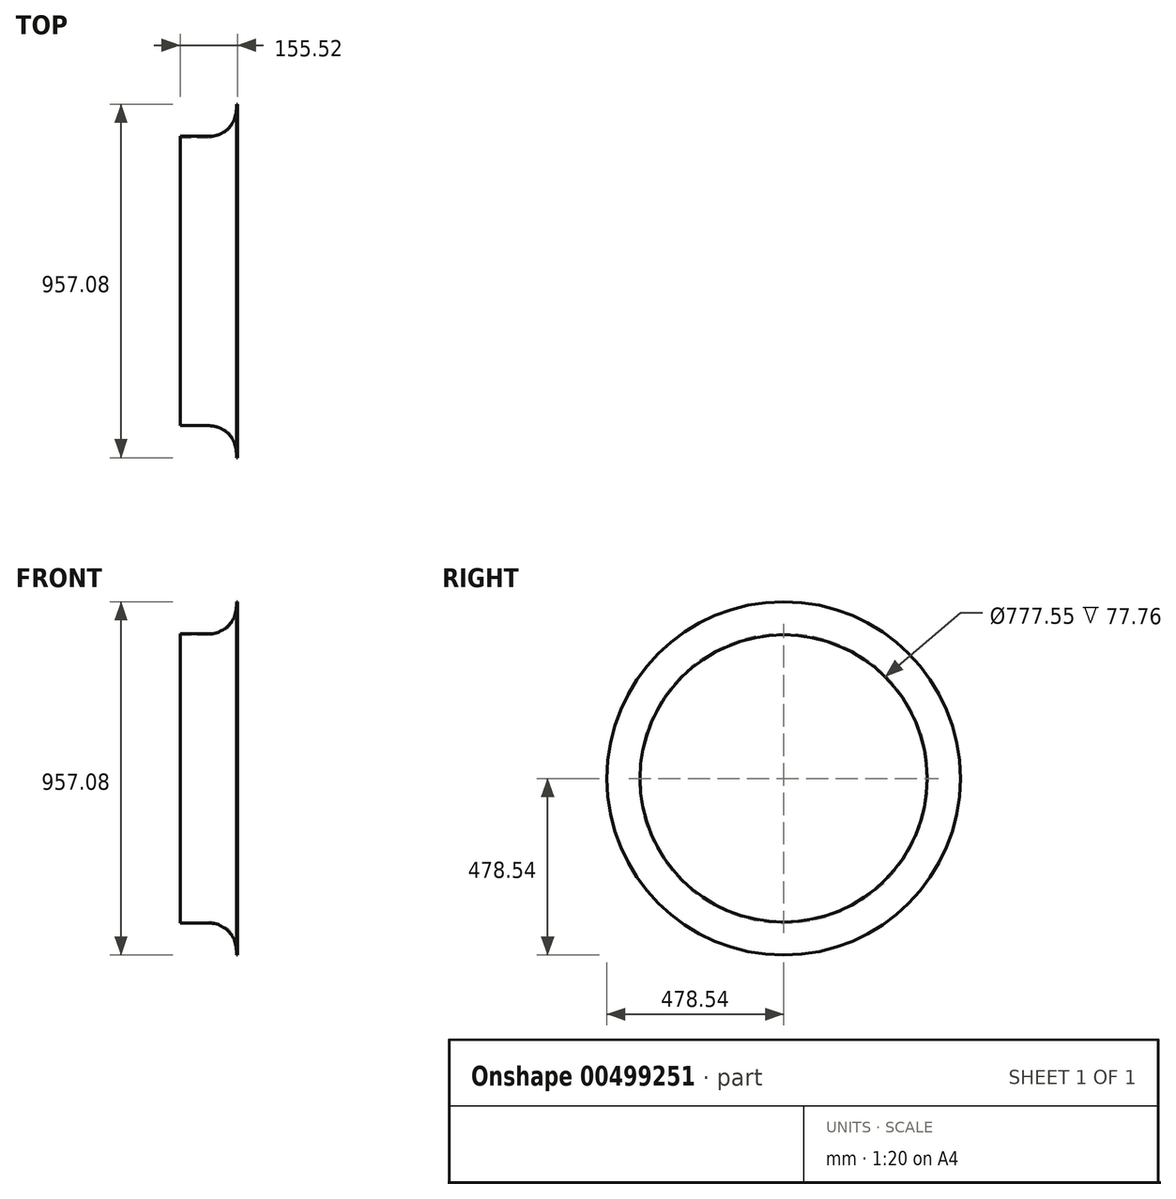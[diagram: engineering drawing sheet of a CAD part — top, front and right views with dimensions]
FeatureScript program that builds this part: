
annotation { "Feature Type Name" : "Feature", "Feature Type Description" : "" }
export const myFeature = defineFeature(function(context is Context, id is Id, definition is map)
    precondition{}
    {
        {
            var Q0;
            Q0=qCreatedBy(makeId("Front.planeOp"),FACE);
            var sketch = newSketch(context, id + "F0", { "sketchPlane" : qUnion([Q0])});
            skLineSegment(sketch, "E0", {"start": v(0, 478.53) * mm, "end": v(0, 466.53) * mm});
            skLineSegment(sketch, "E1", {"start": v(-77.76, 388.77) * mm, "end": v(-155.52, 388.77) * mm});
            skPoint(sketch, "E2.visualSharp", {"position": v(0, 388.77) * mm});
            skArc(sketch, "E2.filletArc", {"start": v(-77.76, 388.77) * mm, "mid": v(-22.78, 411.55) * mm, "end": v(0, 466.53) * mm});
            skLineSegment(sketch, "E3", {"start": v(0, 0) * mm, "end": v(-82.46, 0) * mm, "construction": true});
            skLineSegment(sketch, "E4.0", {"start": v(-77.76, 391.77) * mm, "end": v(-155.52, 391.77) * mm});
            skArc(sketch, "E4.1", {"start": v(-77.76, 391.77) * mm, "mid": v(-24.9, 413.67) * mm, "end": v(-3, 466.53) * mm});
            skLineSegment(sketch, "E4.2", {"start": v(-3, 478.53) * mm, "end": v(-3, 466.53) * mm});
            skLineSegment(sketch, "E5", {"start": v(-3, 478.53) * mm, "end": v(0, 478.53) * mm});
            skLineSegment(sketch, "E6", {"start": v(-155.52, 391.77) * mm, "end": v(-155.52, 388.77) * mm});
            skSolve(sketch);
        }
        {
            var Q0;
            Q0 = qSketchRegion(id + "F0", true);
            var Q1;
            Q1=sQuery(id+"F0.wireOp",EDGE,"E3");
            revolve(context, id + "F1", {"entities" : qUnion([Q0]), "axis" : qUnion([Q1]), "revolveType" : RevolveType.FULL});
        }
    });
